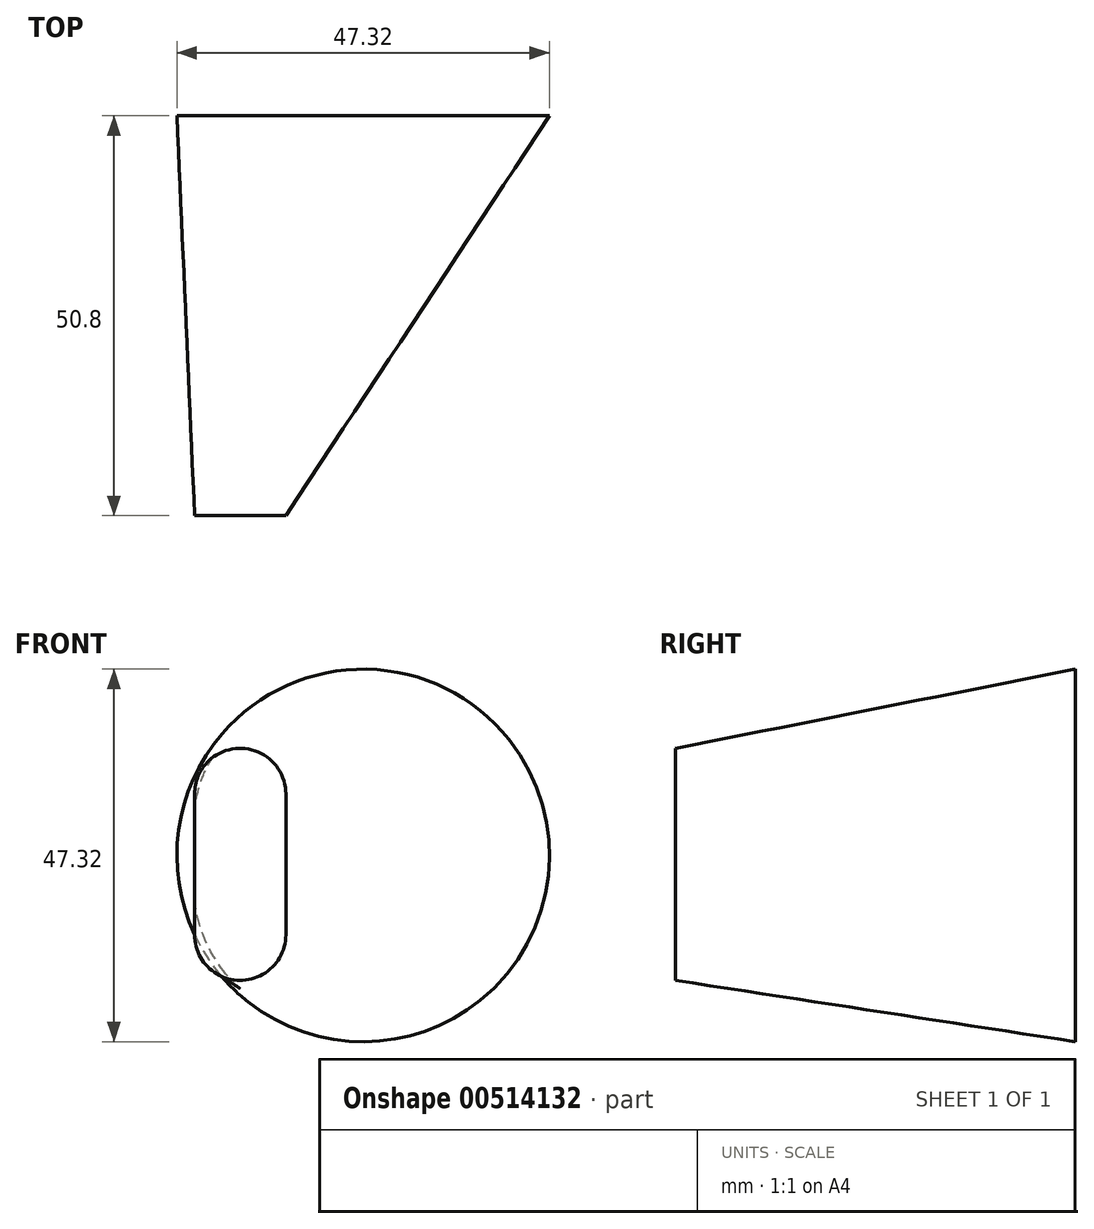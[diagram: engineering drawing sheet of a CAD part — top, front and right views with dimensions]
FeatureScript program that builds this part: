
annotation { "Feature Type Name" : "Feature", "Feature Type Description" : "" }
export const myFeature = defineFeature(function(context is Context, id is Id, definition is map)
    precondition{}
    {
        {
            var Q0;
            Q0=qCreatedBy(makeId("Front.planeOp"),FACE);
            var sketch = newSketch(context, id + "F0", { "sketchPlane" : qUnion([Q0])});
            skArc(sketch, "E0", {"start": v(-17.92, 15.45) * mm, "mid": v(-23.55, -2.28) * mm, "end": v(-14.62, -18.6) * mm});
            skArc(sketch, "E1", {"start": v(18.5, 14.75) * mm, "mid": v(0.46, 23.66) * mm, "end": v(-17.92, 15.45) * mm});
            skArc(sketch, "E2", {"start": v(-14.62, -18.6) * mm, "mid": v(0.15, -23.66) * mm, "end": v(14.86, -18.41) * mm});
            skArc(sketch, "E3", {"start": v(14.86, -18.41) * mm, "mid": v(23.52, -2.59) * mm, "end": v(18.5, 14.75) * mm});
            skPoint(sketch, "E4", {"position": v(0, 23.66) * mm});
            skPoint(sketch, "E5", {"position": v(0, -23.66) * mm});
            skPoint(sketch, "E6", {"position": v(-23.66, 0) * mm});
            skPoint(sketch, "E7", {"position": v(23.66, 0) * mm});
            skPoint(sketch, "E8", {"position": v(21.2, -10.51) * mm});
            skPoint(sketch, "E9", {"position": v(7.53, -22.43) * mm});
            skPoint(sketch, "E10", {"position": v(-7.53, -22.43) * mm});
            skPoint(sketch, "E11", {"position": v(-21.2, -10.51) * mm});
            skPoint(sketch, "E12", {"position": v(-22.2, 8.16) * mm});
            skPoint(sketch, "E13", {"position": v(-9.6, 21.63) * mm});
            skPoint(sketch, "E14", {"position": v(9.6, 21.63) * mm});
            skPoint(sketch, "E15", {"position": v(22.2, 8.17) * mm});
            skSolve(sketch);
        }
        {
            var Q0;
            Q0=qCreatedBy(makeId("Front.planeOp"),FACE);
            cPlane(context, id + "F1", {"entities" : qUnion([Q0]), "cplaneType" : CPlaneType.OFFSET, "offset" : 50.8 * mm, "width" : 152.4 * mm, "height" : 152.4 * mm});
        }
        {
            var Q0;
            Q0=qCreatedBy(id+"F1.planeOp",FACE);
            var sketch = newSketch(context, id + "F2", { "sketchPlane" : qUnion([Q0])});
            skLineSegment(sketch, "E16.bottom", {"start": v(-21.41, -10.08) * mm, "end": v(-9.82, -10.08) * mm});
            skLineSegment(sketch, "E16.top", {"start": v(-21.41, 7.8) * mm, "end": v(-9.82, 7.8) * mm});
            skLineSegment(sketch, "E16.left", {"start": v(-21.41, -10.08) * mm, "end": v(-21.41, 7.8) * mm});
            skLineSegment(sketch, "E16.right", {"start": v(-9.82, -10.08) * mm, "end": v(-9.82, 7.8) * mm});
            skArc(sketch, "E17", {"start": v(-9.82, 7.8) * mm, "mid": v(-15.62, 13.6) * mm, "end": v(-21.41, 7.8) * mm});
            skArc(sketch, "E18", {"start": v(-21.41, -10.08) * mm, "mid": v(-15.62, -15.87) * mm, "end": v(-9.82, -10.08) * mm});
            skSolve(sketch);
        }
        {
            var Q0;
            Q0 = qSketchRegion(id + "F2", true);
            var Q1;
            Q1 = qSketchRegion(id + "F0", true);
            loft(context, id + "F3", {"sheetProfilesArray" : [{ "sheetProfileEntities" : qUnion([Q0]) }, { "sheetProfileEntities" : qUnion([Q1]) }]});
        }
    });
